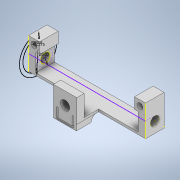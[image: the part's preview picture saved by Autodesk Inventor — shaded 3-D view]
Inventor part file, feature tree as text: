
AUTODESK INVENTOR PART (.ipt)
format: ipt  version: 2020 (Build 240168000, 168)  size: 284,160 bytes
history: native  units: mm
features: sketch x25, extrude x15, fillet x1
ambient origin geometry x8: Origin, YZ Plane, XZ Plane, XY Plane, X Axis, Y Axis, Z Axis, Center Point
bodies: Solid1 (feature_tree)
feature tree (41):
  sketch  "Sketch1"  dims[d3=25.4mm d4=25.4mm]
  extrude  "Extrusion1"  Depth=25.4mm
  extrude  "Extrusion2"  Depth=10.0mm TaperAngle=0.0deg
  extrude  "Extrusion3"  Depth=15.0mm
  sketch  "Sketch5"  dims[d14=14.85mm d15=0.0mm d16=20.32mm]
  sketch  "Sketch6"  dims[d17=41.275mm d18=2.0mm]
  extrude  "Extrusion4"  Depth=25.4mm TaperAngle=0.0deg
  sketch  "Sketch8"  dims[d24=10.0mm d25=0.0mm d26=15.0mm]
  extrude  "Extrusion5"  Depth=20.32mm
  extrude  "Extrusion6"  Depth=2.0mm
  sketch  "Sketch11"  dims[d32=25.4mm d33=0.0mm d34=7.4mm]
  extrude  "Extrusion7"  Depth=150.0mm TaperAngle=0.0deg
  extrude  "Extrusion8"  Depth=15.0mm
  extrude  "Extrusion9"  Depth=8.0mm
  sketch  "Sketch14"  dims[d42=25.0mm d43=10.0mm d44=0.0mm]
  sketch  "Sketch15"  dims[d45=31.75mm d46=10.0mm d47=0.0mm d48=12.7mm]
  sketch  "Sketch16"  dims[d49=10.0mm d50=0.0mm]
  extrude  "Extrusion10"  Depth=18.0mm
  extrude  "Extrusion11"  Depth=7.4mm
  sketch  "Sketch19"  dims[d59=1.5875mm]
  sketch  "Sketch20"  dims[d60=1.5875mm]
  extrude  "Extrusion12"  Depth=14.9mm TaperAngle=0.0deg
  extrude  "Extrusion13"  Depth=20.0mm TaperAngle=0.0deg
  sketch  "Sketch23"  dims[d63=8.0mm]
  sketch  "Sketch24"  dims[d64=20.0mm d65=0.0mm]
  extrude  "Extrusion14"  Depth=10.0mm TaperAngle=0.0deg
  extrude  "Extrusion15"  Depth=10.0mm TaperAngle=0.0deg
  fillet  "Fillet1"  Radius=12.7mm
  sketch  "Sketch2"  dims[d5=12.7mm d6=10.0mm d7=0.0mm]
  sketch  "Sketch3"  dims[d8=15.0mm d9=15.0mm]
  sketch  "Sketch4"  dims[d10=8.0mm d11=25.4mm d12=0.0mm]
  sketch  "Sketch7"  dims[d19=3.25mm d20=150.0mm d21=10.0mm d22=0.0mm d23=0.0mm]
  sketch  "Sketch9"  dims[d27=15.0mm d28=8.0mm]
  sketch  "Sketch10"  dims[d29=25.4mm d30=0.0mm d31=18.0mm]
  sketch  "Sketch12"  dims[d35=14.9mm d36=0.0mm d37=14.9mm d38=0.0mm]
  sketch  "Sketch13"  dims[d39=31.75mm d40=20.0mm d41=0.0mm]
  sketch  "Sketch17"  dims[d51=21.0mm]
  sketch  "Sketch18"  dims[d58=1.5875mm]
  sketch  "Sketch21"  dims[d61=6.35mm]
  sketch  "Sketch22"  dims[d62=50.8mm]
  sketch  "Sketch25"  dims[d66=15.0mm d67=0.0mm d68=9.0mm]
